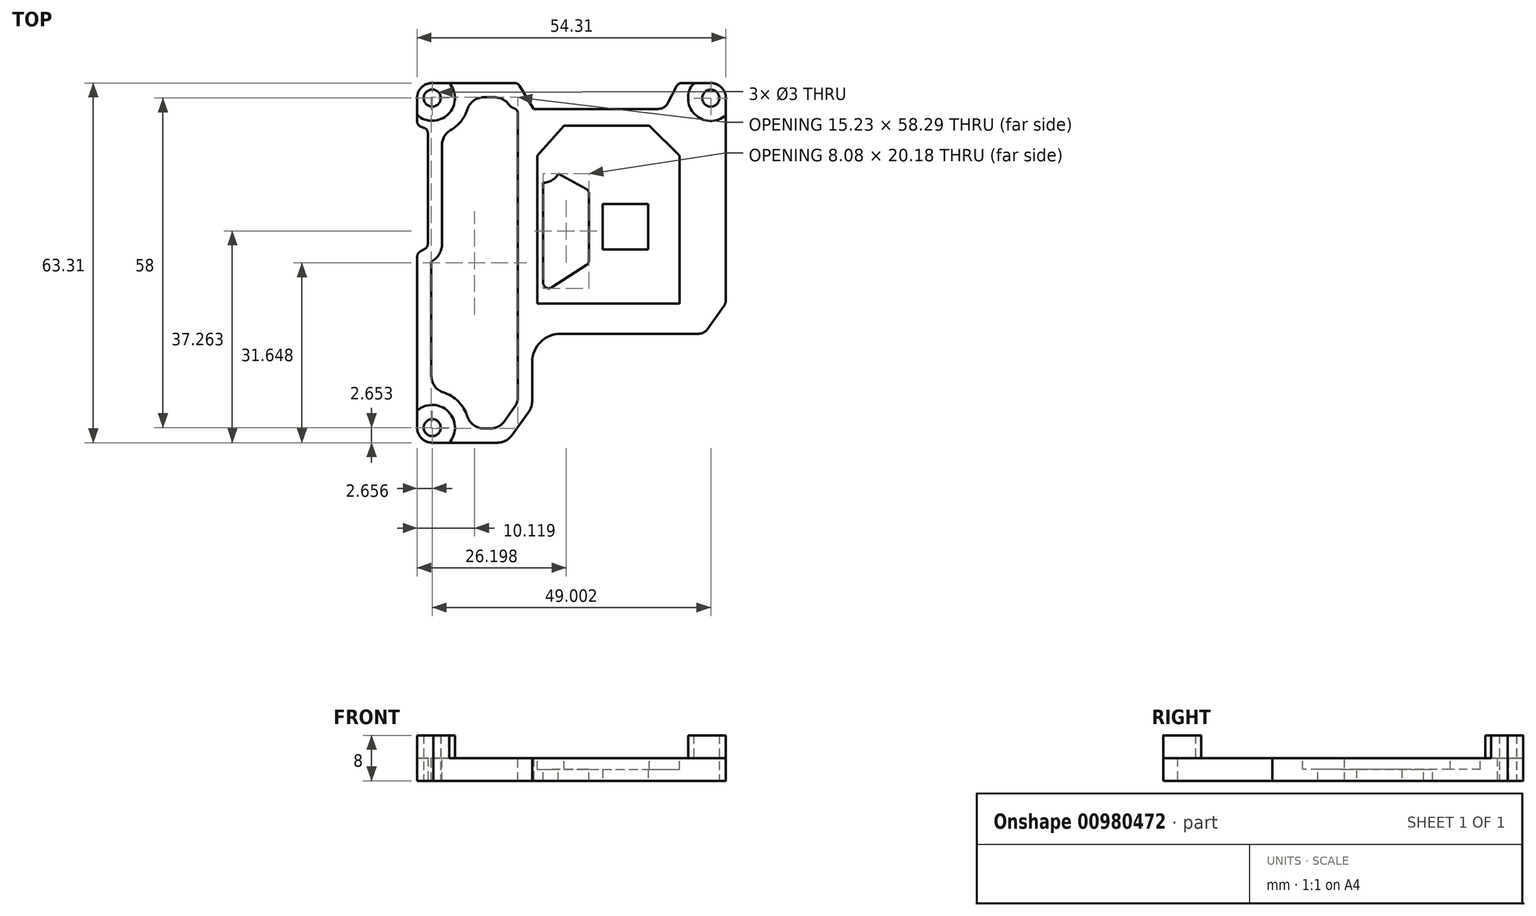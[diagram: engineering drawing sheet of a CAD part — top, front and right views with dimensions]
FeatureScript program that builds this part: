
annotation { "Feature Type Name" : "Feature", "Feature Type Description" : "" }
export const myFeature = defineFeature(function(context is Context, id is Id, definition is map)
    precondition{}
    {
        {
            var Q0;
            Q0=qCreatedBy(makeId("Top.planeOp"),FACE);
            var sketch = newSketch(context, id + "F0", { "sketchPlane" : qUnion([Q0])});
            skLineSegment(sketch, "E0.0.0", {"start": v(13.67, 14.78) * mm, "end": v(-11.33, 14.78) * mm});
            skLineSegment(sketch, "E0.0.1", {"start": v(-11.33, 14.78) * mm, "end": v(-11.33, -11.22) * mm});
            skLineSegment(sketch, "E0.0.2", {"start": v(-11.33, -11.22) * mm, "end": v(13.67, -11.22) * mm});
            skLineSegment(sketch, "E0.0.3", {"start": v(13.67, -11.22) * mm, "end": v(13.67, 14.78) * mm});
            skArc(sketch, "E1.0", {"start": v(-32.49, 24.84) * mm, "mid": v(-31.63, 26.89) * mm, "end": v(-29.51, 27.57) * mm});
            skArc(sketch, "E2.0", {"start": v(19.17, 27.57) * mm, "mid": v(21.07, 26.77) * mm, "end": v(21.82, 24.86) * mm});
            skArc(sketch, "E3.0", {"start": v(-29.65, -35.72) * mm, "mid": v(-31.7, -34.96) * mm, "end": v(-32.49, -32.92) * mm});
            skLineSegment(sketch, "E4.0", {"start": v(8.17, 6.28) * mm, "end": v(8.17, -1.72) * mm});
            skLineSegment(sketch, "E5.0", {"start": v(0.17, 6.28) * mm, "end": v(8.17, 6.28) * mm});
            skLineSegment(sketch, "E6.0", {"start": v(0.17, 6.28) * mm, "end": v(0.17, -1.72) * mm});
            skLineSegment(sketch, "E7.0", {"start": v(0.17, -1.72) * mm, "end": v(8.17, -1.72) * mm});
            skLineSegment(sketch, "E8", {"start": v(-29.51, 27.57) * mm, "end": v(-14.75, 27.57) * mm});
            skLineSegment(sketch, "E9", {"start": v(-32.49, 25.02) * mm, "end": v(-32.49, 20.1) * mm});
            skLineSegment(sketch, "E10", {"start": v(-29.65, -35.72) * mm, "end": v(-16.75, -35.72) * mm});
            skLineSegment(sketch, "E11", {"start": v(21.82, 24.86) * mm, "end": v(21.82, -11.22) * mm});
            skCircle(sketch, "E12", {"center": v(-29.83, 24.93) * mm, "radius": 1.5 * mm});
            skCircle(sketch, "E13", {"center": v(19.17, 24.91) * mm, "radius": 1.5 * mm});
            skCircle(sketch, "E14", {"center": v(-29.83, -33.07) * mm, "radius": 1.5 * mm});
            skLineSegment(sketch, "E15", {"start": v(-32.49, 20.1) * mm, "end": v(-31.3, 19.72) * mm});
            skLineSegment(sketch, "E16", {"start": v(-30.6, 18.76) * mm, "end": v(-30.6, -0.74) * mm});
            skLineSegment(sketch, "E17", {"start": v(-31.1, -1.6) * mm, "end": v(-32.49, -2.4) * mm});
            skLineSegment(sketch, "E18.trimOffspring", {"start": v(-32.49, -2.4) * mm, "end": v(-32.49, -33.07) * mm});
            skPoint(sketch, "E19.visualSharp", {"position": v(-30.6, 19.5) * mm});
            skArc(sketch, "E19.filletArc", {"start": v(-30.6, 18.76) * mm, "mid": v(-30.8, 19.35) * mm, "end": v(-31.3, 19.72) * mm});
            skPoint(sketch, "E20.visualSharp", {"position": v(-30.6, -1.31) * mm});
            skArc(sketch, "E20.filletArc", {"start": v(-31.1, -1.6) * mm, "mid": v(-30.74, -1.23) * mm, "end": v(-30.6, -0.74) * mm});
            skLineSegment(sketch, "E21", {"start": v(-0.8, 23.02) * mm, "end": v(9.88, 23.02) * mm});
            skLineSegment(sketch, "E22", {"start": v(11.66, 24.1) * mm, "end": v(13.43, 27.57) * mm});
            skLineSegment(sketch, "E23.trimOffspring", {"start": v(13.43, 27.57) * mm, "end": v(19.17, 27.57) * mm});
            skPoint(sketch, "E24.visualSharp", {"position": v(11.1, 23.02) * mm});
            skArc(sketch, "E24.filletArc", {"start": v(9.88, 23.02) * mm, "mid": v(10.92, 23.31) * mm, "end": v(11.66, 24.1) * mm});
            skLineSegment(sketch, "E25", {"start": v(18.02, -16.55) * mm, "end": v(-7.26, -16.55) * mm});
            skLineSegment(sketch, "E26", {"start": v(-12.26, -21.55) * mm, "end": v(-12.26, -29.42) * mm});
            skLineSegment(sketch, "E27", {"start": v(-16.75, -35.72) * mm, "end": v(-12.26, -29.42) * mm});
            skLineSegment(sketch, "E28", {"start": v(18.02, -16.55) * mm, "end": v(21.82, -11.22) * mm});
            skPoint(sketch, "E28.endSnap0", {"position": v(1.17, -11.22) * mm});
            skPoint(sketch, "E29.visualSharp", {"position": v(-12.26, -16.55) * mm});
            skArc(sketch, "E29.filletArc", {"start": v(-7.26, -16.55) * mm, "mid": v(-10.8, -18.01) * mm, "end": v(-12.26, -21.55) * mm});
            skLineSegment(sketch, "E30", {"start": v(-14.75, 27.57) * mm, "end": v(-12, 23.02) * mm});
            skLineSegment(sketch, "E31", {"start": v(-12, 23.02) * mm, "end": v(-0.8, 23.02) * mm});
            skSolve(sketch);
        }
        {
            var Q0;
            Q0=makeQuery(id+"F0.imprint","IMPRINT",FACE,{"disambiguationData":[TD([[makeQuery(id+"F0.imprint","IMPRINT",EDGE,{"derivedFrom":sQuery(id+"F0.wireOp",EDGE,"E0.0.0")}),-1.0]])]});
            var sketch = newSketch(context, id + "F1", { "sketchPlane" : qUnion([Q0])});
            skLineSegment(sketch, "E32.bottom", {"start": v(-11.33, 14.78) * mm, "end": v(13.67, 14.78) * mm});
            skLineSegment(sketch, "E32.top", {"start": v(-11.33, -11.22) * mm, "end": v(13.67, -11.22) * mm});
            skLineSegment(sketch, "E32.left", {"start": v(-11.33, 14.78) * mm, "end": v(-11.33, -11.22) * mm});
            skLineSegment(sketch, "E32.right", {"start": v(13.67, 14.78) * mm, "end": v(13.67, -11.22) * mm});
            skSolve(sketch);
        }
        {
            var Q0;
            Q0 = qSketchRegion(id + "F0", true);
            var Q1;
            Q1=makeQuery(id+"F0.imprint","IMPRINT",FACE,{"disambiguationData":[TD([[makeQuery(id+"F0.imprint","IMPRINT",EDGE,{"derivedFrom":sQuery(id+"F0.wireOp",EDGE,"E0.0.0")}),1.0]])]});
            extrude(context, id + "F2", {"entities" : qUnion([Q0, Q1]), "depth" : 4 * mm, "offsetDistance" : 25 * mm});
        }
        {
            var Q0;
            Q0=makeQuery(id+"F2.opExtrude","CAP_FACE",FACE,{"disambiguationData":[OSD([sQuery(id+"F0.wireOp",EDGE,"E1.0"),sQuery(id+"F0.wireOp",EDGE,"E2.0"),sQuery(id+"F0.wireOp",EDGE,"E3.0"),sQuery(id+"F0.wireOp",EDGE,"E4.0"),sQuery(id+"F0.wireOp",EDGE,"E5.0"),sQuery(id+"F0.wireOp",EDGE,"E6.0"),sQuery(id+"F0.wireOp",EDGE,"E7.0"),sQuery(id+"F0.wireOp",EDGE,"E8"),sQuery(id+"F0.wireOp",EDGE,"E9"),sQuery(id+"F0.wireOp",EDGE,"E10"),sQuery(id+"F0.wireOp",EDGE,"E11"),sQuery(id+"F0.wireOp",EDGE,"E12"),sQuery(id+"F0.wireOp",EDGE,"E13"),sQuery(id+"F0.wireOp",EDGE,"E14"),sQuery(id+"F0.wireOp",EDGE,"E15"),sQuery(id+"F0.wireOp",EDGE,"E16"),sQuery(id+"F0.wireOp",EDGE,"E17"),sQuery(id+"F0.wireOp",EDGE,"E18.trimOffspring"),sQuery(id+"F0.wireOp",EDGE,"E19.filletArc"),sQuery(id+"F0.wireOp",EDGE,"E20.filletArc"),sQuery(id+"F0.wireOp",EDGE,"AzTaWjzL-7Zo8-v1dT-gUMB-ptaIZ0hRT0jZ"),sQuery(id+"F0.wireOp",EDGE,"E21"),sQuery(id+"F0.wireOp",EDGE,"E22"),sQuery(id+"F0.wireOp",EDGE,"E23.trimOffspring"),sQuery(id+"F0.wireOp",EDGE,"E24.filletArc"),sQuery(id+"F0.wireOp",EDGE,"22df945d-a6fd-4e29-b713-8438f0840ca9.filletArc"),sQuery(id+"F0.wireOp",EDGE,"E25"),sQuery(id+"F0.wireOp",EDGE,"E26"),sQuery(id+"F0.wireOp",EDGE,"E27"),sQuery(id+"F0.wireOp",EDGE,"E28"),sQuery(id+"F0.wireOp",EDGE,"E29.filletArc")])],"isStart":false});
            var sketch = newSketch(context, id + "F3", { "sketchPlane" : qUnion([Q0])});
            skLineSegment(sketch, "E33.bottom", {"start": v(-11.33, 14.78) * mm, "end": v(13.67, 14.78) * mm});
            skLineSegment(sketch, "E33.top", {"start": v(-11.33, -11.22) * mm, "end": v(13.67, -11.22) * mm});
            skLineSegment(sketch, "E33.left", {"start": v(-11.33, 14.78) * mm, "end": v(-11.33, -11.22) * mm});
            skLineSegment(sketch, "E33.right", {"start": v(13.67, 14.78) * mm, "end": v(13.67, -11.22) * mm});
            skSolve(sketch);
        }
        {
            var Q0;
            Q0=makeQuery(id+"F3.imprint","IMPRINT",FACE,{"disambiguationData":[TD([[makeQuery(id+"F3.imprint","IMPRINT",EDGE,{"derivedFrom":sQuery(id+"F3.wireOp",EDGE,"E33.bottom")}),-1.0]])]});
            extrude(context, id + "F4", {"entities" : qUnion([Q0]), "operationType" : NewBodyOperationType.REMOVE, "oppositeDirection" : true, "depth" : 2 * mm, "offsetDistance" : 25 * mm});
        }
        {
            var Q0;
            Q0=makeQuery(id+"F2.opExtrude","CAP_FACE",FACE,{"disambiguationData":[OSD([sQuery(id+"F0.wireOp",EDGE,"E1.0"),sQuery(id+"F0.wireOp",EDGE,"E2.0"),sQuery(id+"F0.wireOp",EDGE,"E3.0"),sQuery(id+"F0.wireOp",EDGE,"E4.0"),sQuery(id+"F0.wireOp",EDGE,"E5.0"),sQuery(id+"F0.wireOp",EDGE,"E6.0"),sQuery(id+"F0.wireOp",EDGE,"E7.0"),sQuery(id+"F0.wireOp",EDGE,"E8"),sQuery(id+"F0.wireOp",EDGE,"E9"),sQuery(id+"F0.wireOp",EDGE,"E10"),sQuery(id+"F0.wireOp",EDGE,"E11"),sQuery(id+"F0.wireOp",EDGE,"E12"),sQuery(id+"F0.wireOp",EDGE,"E13"),sQuery(id+"F0.wireOp",EDGE,"E14"),sQuery(id+"F0.wireOp",EDGE,"E15"),sQuery(id+"F0.wireOp",EDGE,"E16"),sQuery(id+"F0.wireOp",EDGE,"E17"),sQuery(id+"F0.wireOp",EDGE,"E18.trimOffspring"),sQuery(id+"F0.wireOp",EDGE,"E19.filletArc"),sQuery(id+"F0.wireOp",EDGE,"E20.filletArc"),sQuery(id+"F0.wireOp",EDGE,"AzTaWjzL-7Zo8-v1dT-gUMB-ptaIZ0hRT0jZ"),sQuery(id+"F0.wireOp",EDGE,"E21"),sQuery(id+"F0.wireOp",EDGE,"E22"),sQuery(id+"F0.wireOp",EDGE,"E23.trimOffspring"),sQuery(id+"F0.wireOp",EDGE,"E24.filletArc"),sQuery(id+"F0.wireOp",EDGE,"22df945d-a6fd-4e29-b713-8438f0840ca9.filletArc"),sQuery(id+"F0.wireOp",EDGE,"E25"),sQuery(id+"F0.wireOp",EDGE,"E26"),sQuery(id+"F0.wireOp",EDGE,"E27"),sQuery(id+"F0.wireOp",EDGE,"E28"),sQuery(id+"F0.wireOp",EDGE,"E29.filletArc")])],"isStart":false});
            var sketch = newSketch(context, id + "F5", { "sketchPlane" : qUnion([Q0])});
            skArc(sketch, "E34.0.0", {"start": v(-29.51, 27.57) * mm, "mid": v(-31.63, 26.89) * mm, "end": v(-32.49, 24.84) * mm});
            skLineSegment(sketch, "E34.0.1", {"start": v(-32.49, 24.84) * mm, "end": v(-32.49, 21.94) * mm});
            skLineSegment(sketch, "E34.0.7", {"start": v(-32.49, -30.07) * mm, "end": v(-32.49, -32.92) * mm});
            skArc(sketch, "E34.0.8", {"start": v(-32.49, -32.92) * mm, "mid": v(-31.7, -34.96) * mm, "end": v(-29.65, -35.72) * mm});
            skLineSegment(sketch, "E34.0.9", {"start": v(-29.65, -35.72) * mm, "end": v(-26.84, -35.72) * mm});
            skLineSegment(sketch, "E34.0.15", {"start": v(21.82, 21.92) * mm, "end": v(21.82, 24.86) * mm});
            skArc(sketch, "E34.0.16", {"start": v(21.82, 24.86) * mm, "mid": v(21.07, 26.77) * mm, "end": v(19.17, 27.57) * mm});
            skLineSegment(sketch, "E34.0.17", {"start": v(19.17, 27.57) * mm, "end": v(16.18, 27.57) * mm});
            skLineSegment(sketch, "E34.0.23", {"start": v(-26.82, 27.57) * mm, "end": v(-29.51, 27.57) * mm});
            skArc(sketch, "E35.0", {"start": v(-32.49, 21.94) * mm, "mid": v(-27.01, 22.1) * mm, "end": v(-26.82, 27.57) * mm});
            skPoint(sketch, "E34.0.2.start.orphan", {"position": v(-32.49, 20.1) * mm});
            skPoint(sketch, "E34.0.3.end.orphan", {"position": v(-30.6, 18.76) * mm});
            skPoint(sketch, "E34.0.3.start.orphan", {"position": v(-31.3, 19.72) * mm});
            skPoint(sketch, "E34.0.22.end.orphan", {"position": v(-5.17, 27.57) * mm});
            skPoint(sketch, "E34.0.21.end.orphan", {"position": v(-2.41, 23.81) * mm});
            skPoint(sketch, "E34.0.20.end.orphan", {"position": v(9.88, 23.02) * mm});
            skArc(sketch, "E36.0", {"start": v(16.18, 27.57) * mm, "mid": v(16.34, 22.09) * mm, "end": v(21.82, 21.92) * mm});
            skArc(sketch, "E37.0", {"start": v(-26.84, -35.72) * mm, "mid": v(-27, -30.24) * mm, "end": v(-32.49, -30.07) * mm});
            skPoint(sketch, "E38.orphan", {"position": v(-32.49, -2.4) * mm});
            skPoint(sketch, "E34.0.10.start.orphan", {"position": v(-16.75, -35.72) * mm});
            skPoint(sketch, "E34.0.11.start.orphan", {"position": v(-12.26, -29.42) * mm});
            skPoint(sketch, "E34.0.12.start.orphan", {"position": v(-12.26, -21.55) * mm});
            skPoint(sketch, "E34.0.13.start.orphan", {"position": v(-7.26, -16.55) * mm});
            skPoint(sketch, "E34.0.14.start.orphan", {"position": v(18.02, -16.55) * mm});
            skPoint(sketch, "E39.orphan", {"position": v(21.82, -11.22) * mm});
            skPoint(sketch, "E34.0.18.start.orphan", {"position": v(13.43, 27.57) * mm});
            skPoint(sketch, "E34.0.19.end.orphan", {"position": v(9.88, 23.02) * mm});
            skPoint(sketch, "E34.0.19.start.orphan", {"position": v(11.66, 24.1) * mm});
            skPoint(sketch, "E34.0.5.end.orphan", {"position": v(-31.1, -1.6) * mm});
            skPoint(sketch, "E34.0.5.start.orphan", {"position": v(-30.6, -0.74) * mm});
            skCircle(sketch, "E40.0", {"center": v(-29.83, 24.93) * mm, "radius": 1.5 * mm});
            skCircle(sketch, "E41.0", {"center": v(19.17, 24.91) * mm, "radius": 1.5 * mm});
            skCircle(sketch, "E42.0", {"center": v(-29.83, -33.07) * mm, "radius": 1.5 * mm});
            skSolve(sketch);
        }
        {
            var Q0;
            Q0 = qSketchRegion(id + "F5", true);
            extrude(context, id + "F6", {"entities" : qUnion([Q0]), "operationType" : NewBodyOperationType.ADD, "depth" : 4 * mm, "offsetDistance" : 25 * mm});
        }
        {
            var Q0;
            Q0=makeQuery(id+"F4.boolean.opBoolean","COPY",FACE,{"derivedFrom":makeQuery(id+"F4.opExtrude","CAP_FACE",FACE,{"disambiguationData":[OSD([sQuery(id+"F0.wireOp",EDGE,"E4.0"),sQuery(id+"F0.wireOp",EDGE,"E5.0"),sQuery(id+"F0.wireOp",EDGE,"E6.0"),sQuery(id+"F0.wireOp",EDGE,"E7.0"),sQuery(id+"F3.wireOp",EDGE,"E33.bottom"),sQuery(id+"F3.wireOp",EDGE,"E33.top"),sQuery(id+"F3.wireOp",EDGE,"E33.left"),sQuery(id+"F3.wireOp",EDGE,"E33.right")])],"isStart":false})});
            var sketch = newSketch(context, id + "F7", { "sketchPlane" : qUnion([Q0])});
            skLineSegment(sketch, "E43.4", {"start": v(-14.76, -28.62) * mm, "end": v(-14.76, -21.55) * mm});
            skLineSegment(sketch, "E43.6", {"start": v(-18.04, -33.22) * mm, "end": v(-14.76, -28.62) * mm});
            skLineSegment(sketch, "E43.7", {"start": v(-23.34, -33.22) * mm, "end": v(-18.04, -33.22) * mm});
            skArc(sketch, "E43.8", {"start": v(-29.99, -26.57) * mm, "mid": v(-25.24, -28.47) * mm, "end": v(-23.34, -33.22) * mm});
            skLineSegment(sketch, "E43.13", {"start": v(-16.81, 25.07) * mm, "end": v(-23.33, 25.07) * mm});
            skArc(sketch, "E43.14", {"start": v(-23.33, 25.07) * mm, "mid": v(-24.62, 21.05) * mm, "end": v(-28.1, 18.67) * mm});
            skLineSegment(sketch, "E43.15", {"start": v(-28.1, 18.67) * mm, "end": v(-28.1, -0.74) * mm});
            skArc(sketch, "E43.16", {"start": v(-28.1, -0.74) * mm, "mid": v(-28.57, -2.48) * mm, "end": v(-29.84, -3.76) * mm});
            skLineSegment(sketch, "E43.17", {"start": v(-29.84, -3.76) * mm, "end": v(-29.99, -3.84) * mm});
            skLineSegment(sketch, "E43.18", {"start": v(-29.99, -3.84) * mm, "end": v(-29.99, -26.57) * mm});
            skLineSegment(sketch, "E44", {"start": v(-14.76, -21.55) * mm, "end": v(-14.76, 23.02) * mm});
            skArc(sketch, "E45", {"start": v(-16.81, 25.07) * mm, "mid": v(-16.2, 23.62) * mm, "end": v(-14.76, 23.02) * mm});
            skPoint(sketch, "E46.0.end.orphan", {"position": v(13.67, -11.22) * mm});
            skPoint(sketch, "E46.0.start.orphan", {"position": v(13.67, 14.78) * mm});
            skLineSegment(sketch, "E47.0", {"start": v(-2.25, 8.69) * mm, "end": v(-7.65, 11.63) * mm});
            skLineSegment(sketch, "E47.1", {"start": v(-2.25, -4.17) * mm, "end": v(-2.25, 8.69) * mm});
            skLineSegment(sketch, "E47.2", {"start": v(-2.25, -4.17) * mm, "end": v(-10.33, -9.38) * mm});
            skLineSegment(sketch, "E47.3", {"start": v(-10.33, 10.04) * mm, "end": v(-10.33, -9.38) * mm});
            skLineSegment(sketch, "E48.0", {"start": v(-0.56, 9.98) * mm, "end": v(10.72, 9.98) * mm});
            skLineSegment(sketch, "E48.1", {"start": v(-1.52, 10.23) * mm, "end": v(-7.29, 13.37) * mm});
            skLineSegment(sketch, "E48.2", {"start": v(-7.44, 14.08) * mm, "end": v(12.58, 14.08) * mm});
            skLineSegment(sketch, "E48.3", {"start": v(10.72, 9.98) * mm, "end": v(12.58, 14.08) * mm});
            skLineSegment(sketch, "E49.0", {"start": v(-0.96, -5.72) * mm, "end": v(10.48, -5.72) * mm});
            skLineSegment(sketch, "E49.1", {"start": v(-0.96, -5.72) * mm, "end": v(-7.94, -10.22) * mm});
            skLineSegment(sketch, "E49.2", {"start": v(-7.94, -10.22) * mm, "end": v(12.21, -10.22) * mm});
            skLineSegment(sketch, "E49.3", {"start": v(10.48, -5.72) * mm, "end": v(12.21, -10.22) * mm});
            skPoint(sketch, "E50.0.end.orphan", {"position": v(-11.33, -11.22) * mm});
            skPoint(sketch, "E50.0.start.orphan", {"position": v(-11.33, 14.78) * mm});
            skPoint(sketch, "E51.visualSharp", {"position": v(-1.07, 9.98) * mm});
            skArc(sketch, "E51.filletArc", {"start": v(-1.52, 10.23) * mm, "mid": v(-1.06, 10.05) * mm, "end": v(-0.56, 9.98) * mm});
            skArc(sketch, "E52", {"start": v(-10.33, 10.04) * mm, "mid": v(-8.77, 10.47) * mm, "end": v(-7.65, 11.63) * mm});
            skArc(sketch, "E53.trimOffspring", {"start": v(-7.29, 13.37) * mm, "mid": v(-7.34, 13.73) * mm, "end": v(-7.44, 14.08) * mm});
            skSolve(sketch);
        }
        {
            var Q0;
            Q0=makeQuery(id+"F7.imprint","IMPRINT",FACE,{"disambiguationData":[TD([[makeQuery(id+"F7.imprint","IMPRINT",EDGE,{"derivedFrom":sQuery(id+"F7.wireOp",EDGE,"E43.4")}),1.0]])]});
            var Q1;
            Q1=makeQuery(id+"F7.imprint","IMPRINT",FACE,{"disambiguationData":[TD([[makeQuery(id+"F7.imprint","IMPRINT",EDGE,{"derivedFrom":sQuery(id+"F7.wireOp",EDGE,"E47.0")}),1.0]])]});
            extrude(context, id + "F8", {"entities" : qUnion([Q0, Q1]), "operationType" : NewBodyOperationType.REMOVE, "endBound" : BoundingType.THROUGH_ALL, "oppositeDirection" : true, "depth" : 25 * mm, "offsetDistance" : 25 * mm, "hasSecondDirection" : true, "secondDirectionOppositeDirection" : false, "secondDirectionDepth" : 25 * mm});
        }
        {
            var Q0;
            Q0=makeQuery(id+"F2.opExtrude","SWEPT_EDGE",EDGE,{"disambiguationData":[OSD([sQuery(id+"F0.wireOp",EDGE,"E25"),sQuery(id+"F0.wireOp",EDGE,"E28")])]});
            var Q1;
            Q1=makeQuery(id+"F2.opExtrude","SWEPT_EDGE",EDGE,{"disambiguationData":[OSD([sQuery(id+"F0.wireOp",EDGE,"E11"),sQuery(id+"F0.wireOp",EDGE,"E28")])]});
            fillet(context, id + "F9", {"entities" : qUnion([Q0, Q1]), "radius" : 2 * mm, "tangentPropagation" : true, "allowEdgeOverflow" : false});
        }
        {
            var Q0;
            Q0=makeQuery(id+"F2.opExtrude","SWEPT_EDGE",EDGE,{"disambiguationData":[OSD([sQuery(id+"F0.wireOp",EDGE,"E10"),sQuery(id+"F0.wireOp",EDGE,"E27")])]});
            var Q1;
            Q1=makeQuery(id+"F2.opExtrude","SWEPT_EDGE",EDGE,{"disambiguationData":[OSD([sQuery(id+"F0.wireOp",EDGE,"E26"),sQuery(id+"F0.wireOp",EDGE,"E27")])]});
            var Q2;
            Q2=makeQuery(id+"F8.boolean.opBoolean","COPY",EDGE,{"derivedFrom":makeQuery(id+"F8.opExtrude","SWEPT_EDGE",EDGE,{"disambiguationData":[OSD([sQuery(id+"F7.wireOp",EDGE,"E43.6"),sQuery(id+"F7.wireOp",EDGE,"E43.7")])]})});
            var Q3;
            Q3=makeQuery(id+"F8.boolean.opBoolean","COPY",EDGE,{"derivedFrom":makeQuery(id+"F8.opExtrude","SWEPT_EDGE",EDGE,{"disambiguationData":[OSD([sQuery(id+"F7.wireOp",EDGE,"E43.4"),sQuery(id+"F7.wireOp",EDGE,"E43.6")])]})});
            var Q4;
            Q4=makeQuery(id+"F8.boolean.opBoolean","COPY",EDGE,{"derivedFrom":makeQuery(id+"F8.opExtrude","SWEPT_EDGE",EDGE,{"disambiguationData":[OSD([sQuery(id+"F7.wireOp",EDGE,"E43.7"),sQuery(id+"F7.wireOp",EDGE,"E43.8")])]})});
            var Q5;
            Q5=makeQuery(id+"F8.boolean.opBoolean","COPY",EDGE,{"derivedFrom":makeQuery(id+"F8.opExtrude","SWEPT_EDGE",EDGE,{"disambiguationData":[OSD([sQuery(id+"F7.wireOp",EDGE,"E43.8"),sQuery(id+"F7.wireOp",EDGE,"E43.18")])]})});
            var Q6;
            Q6=makeQuery(id+"F8.boolean.opBoolean","COPY",EDGE,{"derivedFrom":makeQuery(id+"F8.opExtrude","SWEPT_EDGE",EDGE,{"disambiguationData":[OSD([sQuery(id+"F7.wireOp",EDGE,"E43.14"),sQuery(id+"F7.wireOp",EDGE,"E43.15")])]})});
            var Q7;
            Q7=makeQuery(id+"F8.boolean.opBoolean","COPY",EDGE,{"derivedFrom":makeQuery(id+"F8.opExtrude","SWEPT_EDGE",EDGE,{"disambiguationData":[OSD([sQuery(id+"F7.wireOp",EDGE,"E43.13"),sQuery(id+"F7.wireOp",EDGE,"E43.14")])]})});
            var Q8;
            Q8=makeQuery(id+"F8.boolean.opBoolean","COPY",EDGE,{"derivedFrom":makeQuery(id+"F8.opExtrude","SWEPT_EDGE",EDGE,{"disambiguationData":[OSD([sQuery(id+"F7.wireOp",EDGE,"E43.13"),sQuery(id+"F7.wireOp",EDGE,"E45")])]})});
            fillet(context, id + "F10", {"entities" : qUnion([Q0, Q1, Q2, Q3, Q4, Q5, Q6, Q7, Q8]), "radius" : 3 * mm, "tangentPropagation" : true, "allowEdgeOverflow" : false});
        }
        {
            var Q0;
            Q0=makeQuery(id+"F2.opExtrude","SWEPT_EDGE",EDGE,{"disambiguationData":[OSD([sQuery(id+"F0.wireOp",EDGE,"E17"),sQuery(id+"F0.wireOp",EDGE,"E18.trimOffspring")])]});
            var Q1;
            Q1=makeQuery(id+"F2.opExtrude","SWEPT_EDGE",EDGE,{"disambiguationData":[OSD([sQuery(id+"F0.wireOp",EDGE,"E9"),sQuery(id+"F0.wireOp",EDGE,"E15")])]});
            var Q2;
            Q2=makeQuery(id+"F2.opExtrude","SWEPT_EDGE",EDGE,{"disambiguationData":[OSD([sQuery(id+"F0.wireOp",EDGE,"E8"),sQuery(id+"F0.wireOp",EDGE,"AzTaWjzL-7Zo8-v1dT-gUMB-ptaIZ0hRT0jZ")])]});
            var Q3;
            Q3=makeQuery(id+"F2.opExtrude","SWEPT_EDGE",EDGE,{"disambiguationData":[OSD([sQuery(id+"F0.wireOp",EDGE,"E22"),sQuery(id+"F0.wireOp",EDGE,"E23.trimOffspring")])]});
            fillet(context, id + "F11", {"entities" : qUnion([Q0, Q1, Q2, Q3]), "radius" : 1 * mm, "tangentPropagation" : true, "allowEdgeOverflow" : false});
        }
        {
            var Q0;
            Q0=makeQuery(id+"F8.boolean.opBoolean","COPY",EDGE,{"derivedFrom":makeQuery(id+"F8.opExtrude","SWEPT_EDGE",EDGE,{"disambiguationData":[OSD([sQuery(id+"F7.wireOp",EDGE,"E44"),sQuery(id+"F7.wireOp",EDGE,"E45")])]})});
            fillet(context, id + "F12", {"entities" : qUnion([Q0]), "radius" : 1 * mm, "tangentPropagation" : true, "allowEdgeOverflow" : false});
        }
        {
            var Q0;
            Q0=makeQuery(id+"F8.boolean.opBoolean","COPY",EDGE,{"derivedFrom":makeQuery(id+"F8.opExtrude","SWEPT_EDGE",EDGE,{"disambiguationData":[OSD([sQuery(id+"F7.wireOp",EDGE,"E47.0"),sQuery(id+"F7.wireOp",EDGE,"E47.1")])]})});
            var Q1;
            Q1=makeQuery(id+"F8.boolean.opBoolean","COPY",EDGE,{"derivedFrom":makeQuery(id+"F8.opExtrude","SWEPT_EDGE",EDGE,{"disambiguationData":[OSD([sQuery(id+"F7.wireOp",EDGE,"E47.2"),sQuery(id+"F7.wireOp",EDGE,"E47.3")])]})});
            var Q2;
            Q2=makeQuery(id+"F8.boolean.opBoolean","COPY",EDGE,{"derivedFrom":makeQuery(id+"F8.opExtrude","SWEPT_EDGE",EDGE,{"disambiguationData":[OSD([sQuery(id+"F7.wireOp",EDGE,"E47.1"),sQuery(id+"F7.wireOp",EDGE,"E47.2")])]})});
            var Q3;
            Q3=makeQuery(id+"F8.boolean.opBoolean","COPY",EDGE,{"derivedFrom":makeQuery(id+"F8.opExtrude","SWEPT_EDGE",EDGE,{"disambiguationData":[OSD([sQuery(id+"F7.wireOp",EDGE,"E49.1"),sQuery(id+"F7.wireOp",EDGE,"E49.2")])]})});
            var Q4;
            Q4=makeQuery(id+"F8.boolean.opBoolean","COPY",EDGE,{"derivedFrom":makeQuery(id+"F8.opExtrude","SWEPT_EDGE",EDGE,{"disambiguationData":[OSD([sQuery(id+"F7.wireOp",EDGE,"E49.0"),sQuery(id+"F7.wireOp",EDGE,"E49.1")])]})});
            var Q5;
            Q5=makeQuery(id+"F8.boolean.opBoolean","COPY",EDGE,{"derivedFrom":makeQuery(id+"F8.opExtrude","SWEPT_EDGE",EDGE,{"disambiguationData":[OSD([sQuery(id+"F7.wireOp",EDGE,"E49.2"),sQuery(id+"F7.wireOp",EDGE,"E49.3")])]})});
            var Q6;
            Q6=makeQuery(id+"F8.boolean.opBoolean","COPY",EDGE,{"derivedFrom":makeQuery(id+"F8.opExtrude","SWEPT_EDGE",EDGE,{"disambiguationData":[OSD([sQuery(id+"F7.wireOp",EDGE,"E49.0"),sQuery(id+"F7.wireOp",EDGE,"E49.3")])]})});
            var Q7;
            Q7=makeQuery(id+"F8.boolean.opBoolean","COPY",EDGE,{"derivedFrom":makeQuery(id+"F8.opExtrude","SWEPT_EDGE",EDGE,{"disambiguationData":[OSD([sQuery(id+"F7.wireOp",EDGE,"E48.0"),sQuery(id+"F7.wireOp",EDGE,"E48.3")])]})});
            var Q8;
            Q8=makeQuery(id+"F8.boolean.opBoolean","COPY",EDGE,{"derivedFrom":makeQuery(id+"F8.opExtrude","SWEPT_EDGE",EDGE,{"disambiguationData":[OSD([sQuery(id+"F7.wireOp",EDGE,"E48.2"),sQuery(id+"F7.wireOp",EDGE,"E48.3")])]})});
            fillet(context, id + "F13", {"entities" : qUnion([Q0, Q1, Q2, Q3, Q4, Q5, Q6, Q7, Q8]), "radius" : 1 * mm, "tangentPropagation" : true, "allowEdgeOverflow" : false});
        }
        {
            var Q0;
            Q0=makeQuery(id+"F2.opExtrude","CAP_FACE",FACE,{"disambiguationData":[OSD([sQuery(id+"F0.wireOp",EDGE,"E1.0"),sQuery(id+"F0.wireOp",EDGE,"E2.0"),sQuery(id+"F0.wireOp",EDGE,"E3.0"),sQuery(id+"F0.wireOp",EDGE,"E4.0"),sQuery(id+"F0.wireOp",EDGE,"E5.0"),sQuery(id+"F0.wireOp",EDGE,"E6.0"),sQuery(id+"F0.wireOp",EDGE,"E7.0"),sQuery(id+"F0.wireOp",EDGE,"E8"),sQuery(id+"F0.wireOp",EDGE,"E9"),sQuery(id+"F0.wireOp",EDGE,"E10"),sQuery(id+"F0.wireOp",EDGE,"E11"),sQuery(id+"F0.wireOp",EDGE,"E12"),sQuery(id+"F0.wireOp",EDGE,"E13"),sQuery(id+"F0.wireOp",EDGE,"E14"),sQuery(id+"F0.wireOp",EDGE,"E15"),sQuery(id+"F0.wireOp",EDGE,"E16"),sQuery(id+"F0.wireOp",EDGE,"E17"),sQuery(id+"F0.wireOp",EDGE,"E18.trimOffspring"),sQuery(id+"F0.wireOp",EDGE,"E19.filletArc"),sQuery(id+"F0.wireOp",EDGE,"E20.filletArc"),sQuery(id+"F0.wireOp",EDGE,"AzTaWjzL-7Zo8-v1dT-gUMB-ptaIZ0hRT0jZ"),sQuery(id+"F0.wireOp",EDGE,"E21"),sQuery(id+"F0.wireOp",EDGE,"E22"),sQuery(id+"F0.wireOp",EDGE,"E23.trimOffspring"),sQuery(id+"F0.wireOp",EDGE,"E24.filletArc"),sQuery(id+"F0.wireOp",EDGE,"22df945d-a6fd-4e29-b713-8438f0840ca9.filletArc"),sQuery(id+"F0.wireOp",EDGE,"E25"),sQuery(id+"F0.wireOp",EDGE,"E26"),sQuery(id+"F0.wireOp",EDGE,"E27"),sQuery(id+"F0.wireOp",EDGE,"E28"),sQuery(id+"F0.wireOp",EDGE,"E29.filletArc")])],"isStart":false});
            var sketch = newSketch(context, id + "F14", { "sketchPlane" : qUnion([Q0])});
            skLineSegment(sketch, "E54", {"start": v(-11.33, 14.78) * mm, "end": v(-6.66, 20.06) * mm});
            skLineSegment(sketch, "E55", {"start": v(-6.66, 20.06) * mm, "end": v(8.34, 20.06) * mm});
            skLineSegment(sketch, "E56", {"start": v(8.34, 20.06) * mm, "end": v(13.67, 14.78) * mm});
            skLineSegment(sketch, "E57", {"start": v(-11.33, 14.78) * mm, "end": v(13.67, 14.78) * mm});
            skSolve(sketch);
        }
        {
            var Q0;
            Q0 = qSketchRegion(id + "F14", true);
            extrude(context, id + "F15", {"entities" : qUnion([Q0]), "operationType" : NewBodyOperationType.REMOVE, "oppositeDirection" : true, "depth" : 2 * mm, "offsetDistance" : 25 * mm});
        }
    });
